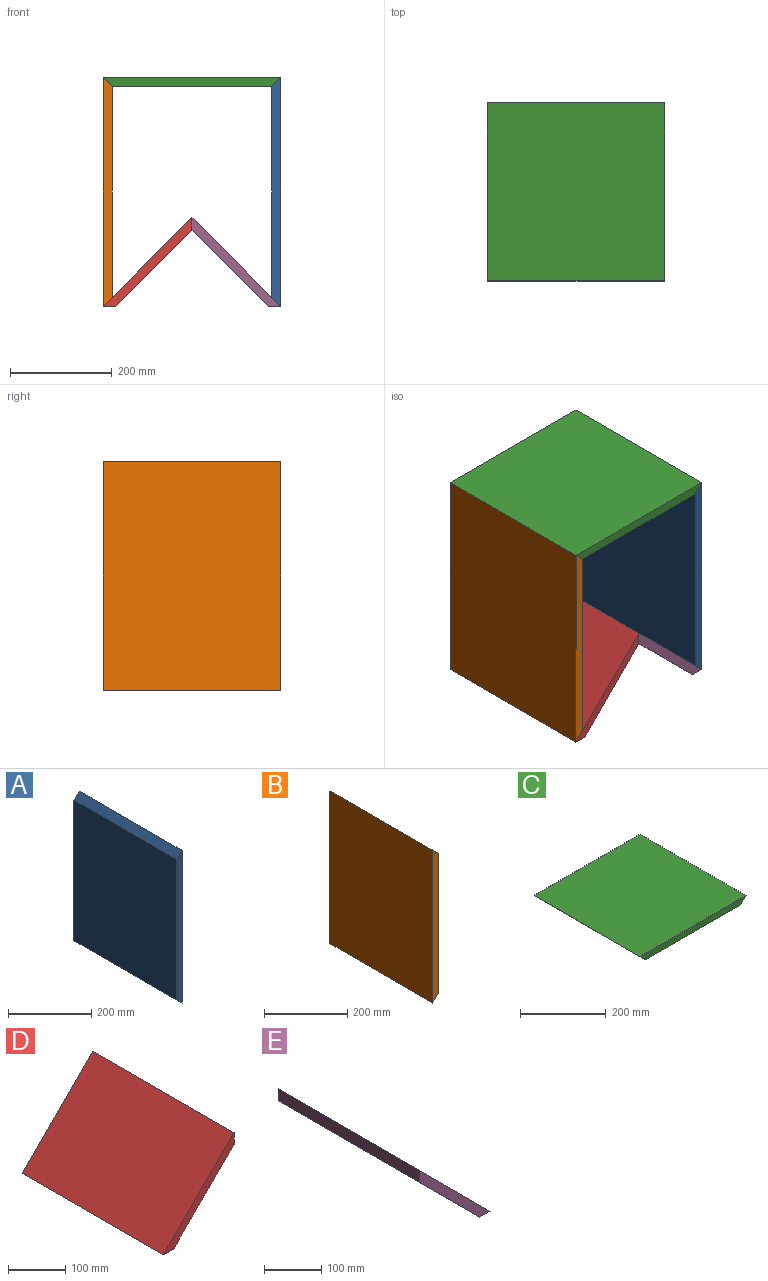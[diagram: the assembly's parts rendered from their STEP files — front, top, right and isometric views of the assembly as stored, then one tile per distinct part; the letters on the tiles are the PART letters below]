
ASSEMBLY  parts=5 mates=4
PART A: 6 faces, bbox 18x350x450 mm
  f0: plane 350x18mm, normal (-0.71,0,-0.71), area 8909.5mm2, adj f1,f3,f4,f5
  f1: plane 450x350mm, normal (1,0,0), area 157500mm2, adj f0,f2,f4,f5
  f2: plane 350x18mm, normal (-0.71,0,0.71), area 8909.5mm2, adj f1,f3,f4,f5
  f3: plane 414x350mm, normal (-1,0,0), area 144900mm2, adj f0,f2,f4,f5
  f4: plane 450x18mm, normal (0,-1,0), area 7776mm2, adj f0,f1,f2,f3
  f5: plane 450x18mm, normal (0,1,0), area 7776mm2, adj f0,f1,f2,f3
PART B: 6 faces, bbox 18x350x450 mm
  f0: plane 450x350mm, normal (-1,0,0), area 157500mm2, adj f1,f3,f4,f5
  f1: plane 350x18mm, normal (0.71,0,-0.71), area 8909.5mm2, adj f0,f2,f4,f5
  f2: plane 414x350mm, normal (1,0,0), area 144900mm2, adj f1,f3,f4,f5
  f3: plane 350x18mm, normal (0.71,0,0.71), area 8909.5mm2, adj f0,f2,f4,f5
  f4: plane 450x18mm, normal (0,-1,0), area 7776mm2, adj f0,f1,f2,f3
  f5: plane 450x18mm, normal (0,1,0), area 7776mm2, adj f0,f1,f2,f3
PART C: 6 faces, bbox 350x350x18 mm
  f0: plane 350x18mm, normal (0,-1,0), area 5976mm2, adj f1,f2,f3,f4
  f1: plane 350x314mm, normal (0,0,-1), area 109900mm2, adj f0,f2,f4,f5
  f2: plane 350x18mm, normal (0.71,0,-0.71), area 8909.5mm2, adj f0,f1,f3,f5
  f3: plane 350x350mm, normal (0,0,1), area 122500mm2, adj f0,f2,f4,f5
  f4: plane 350x18mm, normal (-0.71,0,-0.71), area 8909.5mm2, adj f0,f1,f3,f5
  f5: plane 350x18mm, normal (0,1,0), area 5976mm2, adj f1,f2,f3,f4
PART D: 6 faces, bbox 175x350x175 mm
  f0: plane 175x175mm, normal (0,-1,0), area 4130.8mm2, adj f1,f3,f4,f5
  f1: plane 350x149.54mm, normal (0.71,0,-0.71), area 74020.6mm2, adj f0,f2,f3,f4
  f2: plane 175x175mm, normal (0,1,0), area 4130.8mm2, adj f1,f3,f4,f5
  f3: plane 350x25.46mm, normal (1,0,0), area 8909.5mm2, adj f0,f1,f2,f5
  f4: plane 350x25.46mm, normal (0,0,-1), area 8909.5mm2, adj f0,f1,f2,f5
  f5: plane 350x175mm, normal (-0.71,0,0.71), area 86620.6mm2, adj f0,f2,f3,f4
PART E: 6 faces, bbox 175x350x175 mm
  f0: plane 175x175mm, normal (0,-1,0), area 4130.8mm2, adj f1,f2,f3,f4
  f1: plane 350x149.54mm, normal (-0.71,0,-0.71), area 74020.6mm2, adj f0,f2,f4,f5
  f2: plane 350x25.46mm, normal (0,0,-1), area 8909.5mm2, adj f0,f1,f3,f5
  f3: plane 350x175mm, normal (0.71,0,0.71), area 86620.6mm2, adj f0,f2,f4,f5
  f4: plane 350x25.46mm, normal (-1,0,0), area 8909.5mm2, adj f0,f1,f3,f5
  f5: plane 175x175mm, normal (0,1,0), area 4130.8mm2, adj f1,f2,f3,f4
PLACE A t=(123.86,-172.86,-89.11)mm
PLACE B t=(123.86,-172.86,-89.11)mm
PLACE C t=(123.86,-172.86,-89.11)mm
PLACE D t=(123.86,-172.86,-89.11)mm
PLACE E t=(123.86,-172.86,-89.11)mm
MATE fastened C.f4 <-> B.f3  axis (-0.71,0,-0.71) through (123.86,-522.86,360.89)mm
MATE fastened D.f3 <-> E.f4  axis (1,0,0) through (298.86,-522.86,85.89)mm
MATE fastened B.f1 <-> D.f5  axis (0.71,0,-0.71) through (123.86,-522.86,-89.11)mm
MATE fastened E.f3 <-> A.f0  axis (0.71,0,0.71) through (473.86,-522.86,-89.11)mm
